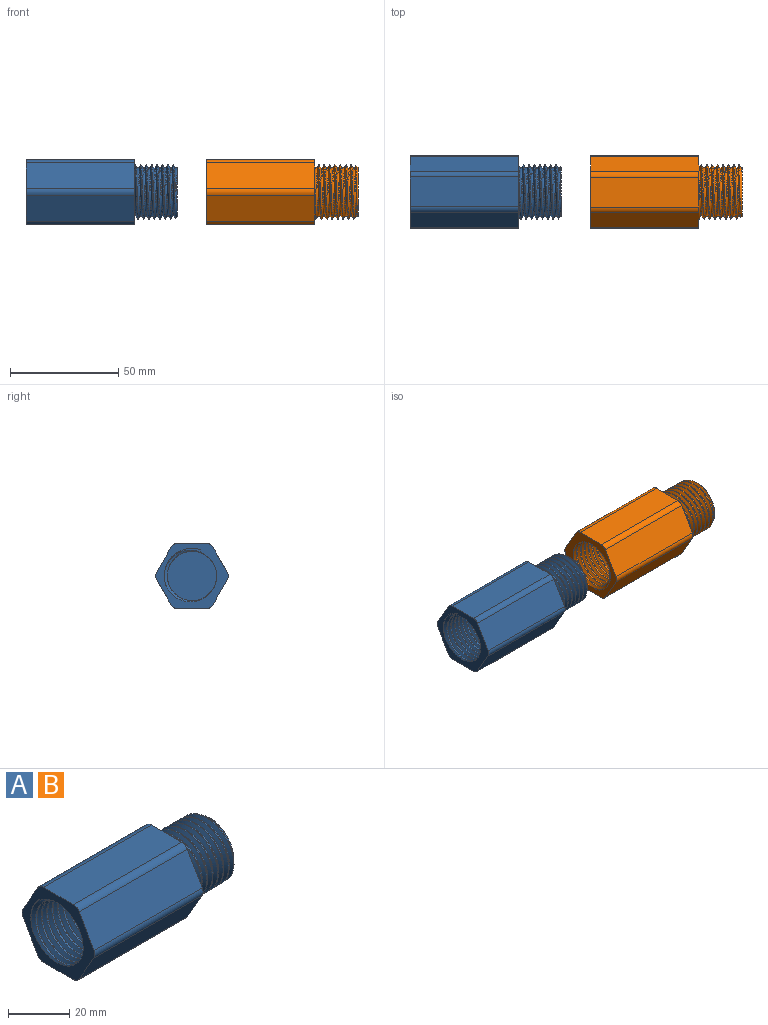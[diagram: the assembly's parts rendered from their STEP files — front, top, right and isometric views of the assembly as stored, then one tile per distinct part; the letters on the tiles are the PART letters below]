
ASSEMBLY  parts=2 mates=1
PART A: 27 faces, bbox 73x34.5x30.8 mm
  f0: cylinder r=11.45mm len=22.89mm, axis (-1,0,0), area 509.7mm2, adj f17,f22,f23,f26
  f1: cylinder r=12.5mm len=25mm, axis (1,0,0), area 299mm2, adj f2,f3,f16,f20
  f2: bspline ~28.87x25mm, area 896mm2, adj f1,f16,f18,f20
  f3: bspline ~28.87x25mm, area 894.9mm2, adj f1,f16,f18,f20
  f4: plane 50x12mm, normal (0,0.87,-0.5), area 692.8mm2, adj f5,f15,f16,f17
  f5: cylinder r=3mm len=50mm, axis (-1,0,0), area 157.1mm2, adj f4,f6,f16,f17
  f6: plane 50x12mm, normal (0,0.87,0.5), area 692.8mm2, adj f5,f7,f16,f17
  f7: cylinder r=3mm len=50mm, axis (-1,0,0), area 157.1mm2, adj f6,f8,f16,f17
  f8: plane 50x13.86mm, normal (0,0,1), area 692.8mm2, adj f7,f9,f16,f17
  f9: cylinder r=3mm len=50mm, axis (-1,0,0), area 157.1mm2, adj f8,f10,f16,f17
  f10: plane 50x12mm, normal (0,-0.87,0.5), area 692.8mm2, adj f9,f11,f16,f17
  f11: cylinder r=3mm len=50mm, axis (-1,0,0), area 157.1mm2, adj f10,f12,f16,f17
  f12: plane 50x12mm, normal (0,-0.87,-0.5), area 692.8mm2, adj f11,f13,f16,f17
  f13: cylinder r=3mm len=50mm, axis (-1,0,0), area 157.1mm2, adj f12,f14,f16,f17
  f14: plane 50x13.86mm, normal (0,0,-1), area 692.8mm2, adj f13,f15,f16,f17
  f15: cylinder r=3mm len=50mm, axis (-1,0,0), area 157.1mm2, adj f4,f14,f16,f17
  f16: plane 34.49x30.77mm, normal (1,0,0), area 342.8mm2, adj f1,f2,f3,f4,f5,f6,f7,f8
  f17: plane 34.5x30.79mm, normal (-1,0,0), area 320.4mm2, adj f0,f4,f5,f6,f7,f8,f9,f10
  f18: cylinder r=11.15mm len=22.29mm, axis (-1,0,0), area 463.8mm2, adj f2,f3,f16,f19
  f19: plane 22.29x22.29mm, normal (1,0,0), area 390.3mm2, adj f18,f20
  f20: cone r=15.15mm half-angle=45deg, axis (-1,0,0), area 61.6mm2, adj f1,f2,f3,f19
  f21: cylinder r=12.8mm len=25.6mm, axis (1,0,0), area 284.9mm2, adj f17,f22,f23,f24
  f22: bspline ~29.56x25.6mm, area 1104.2mm2, adj f0,f17,f21,f24,f25
  f23: bspline ~29.56x25.78mm, area 1156mm2, adj f0,f17,f21,f24,f25
  f24: plane 1.88x1.35mm, normal (0,0,1), area 1.5mm2, adj f21,f22,f23,f25
  f25: cylinder r=11.45mm len=22.89mm, axis (1,0,0), area 67.6mm2, adj f22,f23,f24,f26
  f26: plane 22.89x22.89mm, normal (-1,0,0), area 411.6mm2, adj f0,f25
PART B: same geometry as A
PLACE A at identity fixed
PLACE B rot(axis=(-1,0,0),179.9deg) t=(83.5,0,0)mm
MATE cylindrical B.f0 <-> A.f18  axis (-1,0,0) through (78.5,0,0)mm
